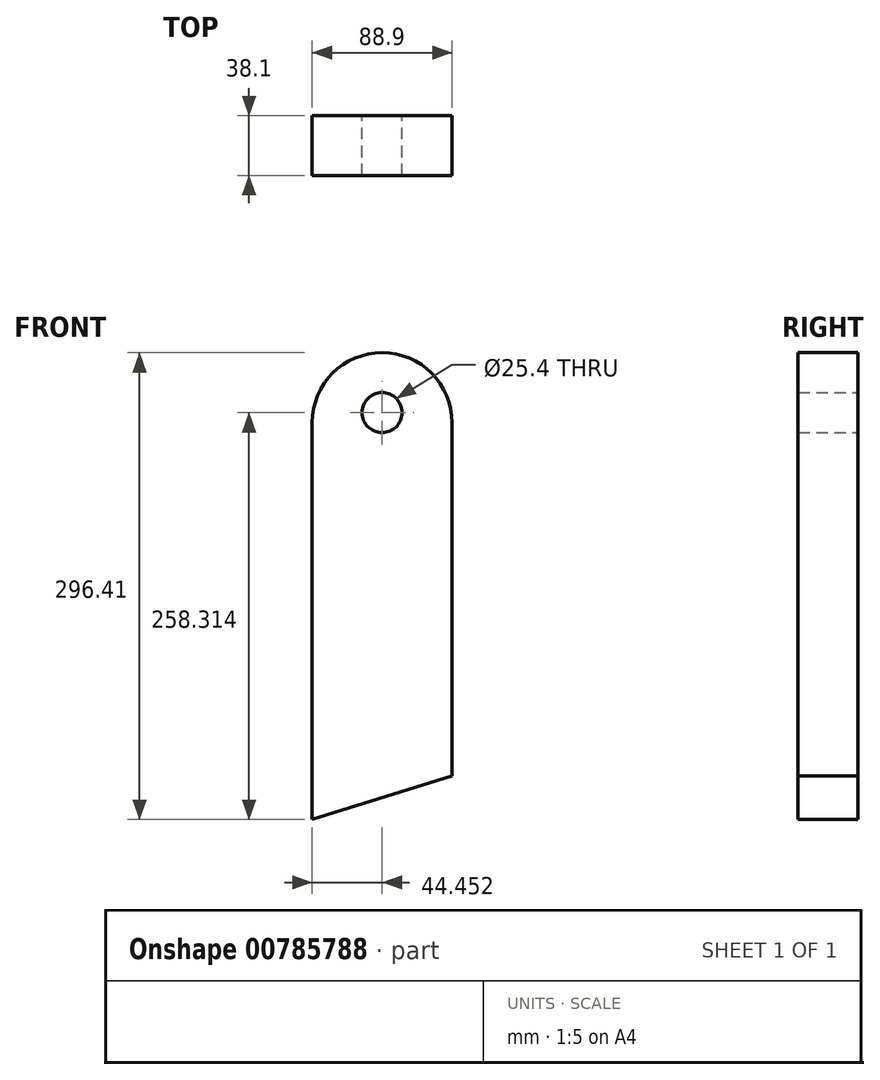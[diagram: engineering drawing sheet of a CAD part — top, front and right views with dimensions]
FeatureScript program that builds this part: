
annotation { "Feature Type Name" : "Feature", "Feature Type Description" : "" }
export const myFeature = defineFeature(function(context is Context, id is Id, definition is map)
    precondition{}
    {
        {
            var Q0;
            Q0=qCreatedBy(makeId("Front.planeOp"),FACE);
            var sketch = newSketch(context, id + "F0", { "sketchPlane" : qUnion([Q0])});
            skLineSegment(sketch, "E0.left", {"start": v(-132.85, 125.47) * mm, "end": v(-132.85, -126.5) * mm});
            skLineSegment(sketch, "E0.right", {"start": v(-43.95, 125.47) * mm, "end": v(-43.95, -98.8) * mm});
            skLineSegment(sketch, "E1", {"start": v(-88.4, 125.47) * mm, "end": v(-88.4, 68.3) * mm, "construction": true});
            skPoint(sketch, "E2", {"position": v(-88.4, 131.82) * mm});
            skLineSegment(sketch, "E3", {"start": v(-132.85, -126.5) * mm, "end": v(-43.95, -98.8) * mm});
            skArc(sketch, "E4", {"start": v(-132.85, 125.47) * mm, "mid": v(-88.4, 169.92) * mm, "end": v(-43.95, 125.47) * mm});
            skSolve(sketch);
        }
        {
            var Q0;
            Q0=makeQuery(id+"F0.imprint","IMPRINT",FACE,{"disambiguationData":[TD([[makeQuery(id+"F0.imprint","IMPRINT",EDGE,{"derivedFrom":sQuery(id+"F0.wireOp",EDGE,"E0.left")}),1.0]])]});
            extrude(context, id + "F1", {"entities" : qUnion([Q0]), "depth" : 38.1 * mm, "offsetDistance" : 25.4 * mm});
        }
        {
            var Q0;
            Q0=sQuery(id+"F0.wireOp",VERTEX,"E2");
            var Q1;
            Q1=makeQuery(id+"F1.opExtrude","SWEPT_BODY",BODY,{"disambiguationData":[OSD([sQuery(id+"F0.wireOp",EDGE,"E0.bottom"),sQuery(id+"F0.wireOp",EDGE,"E0.top"),sQuery(id+"F0.wireOp",EDGE,"E0.left"),sQuery(id+"F0.wireOp",EDGE,"E0.right")])]});
            hole(context, id + "F2", {"style" : HoleStyle.SIMPLE, "endStyle" : HoleEndStyle.THROUGH, "oppositeDirection" : true, "holeDiameter" : 25.4 * mm, "majorDiameter" : 6.35 * mm, "isTappedThrough" : true, "tappedDepth" : 12.7 * mm, "tapClearance" : 3, "locations" : qUnion([Q0]), "scope" : qUnion([Q1])});
        }
    });
